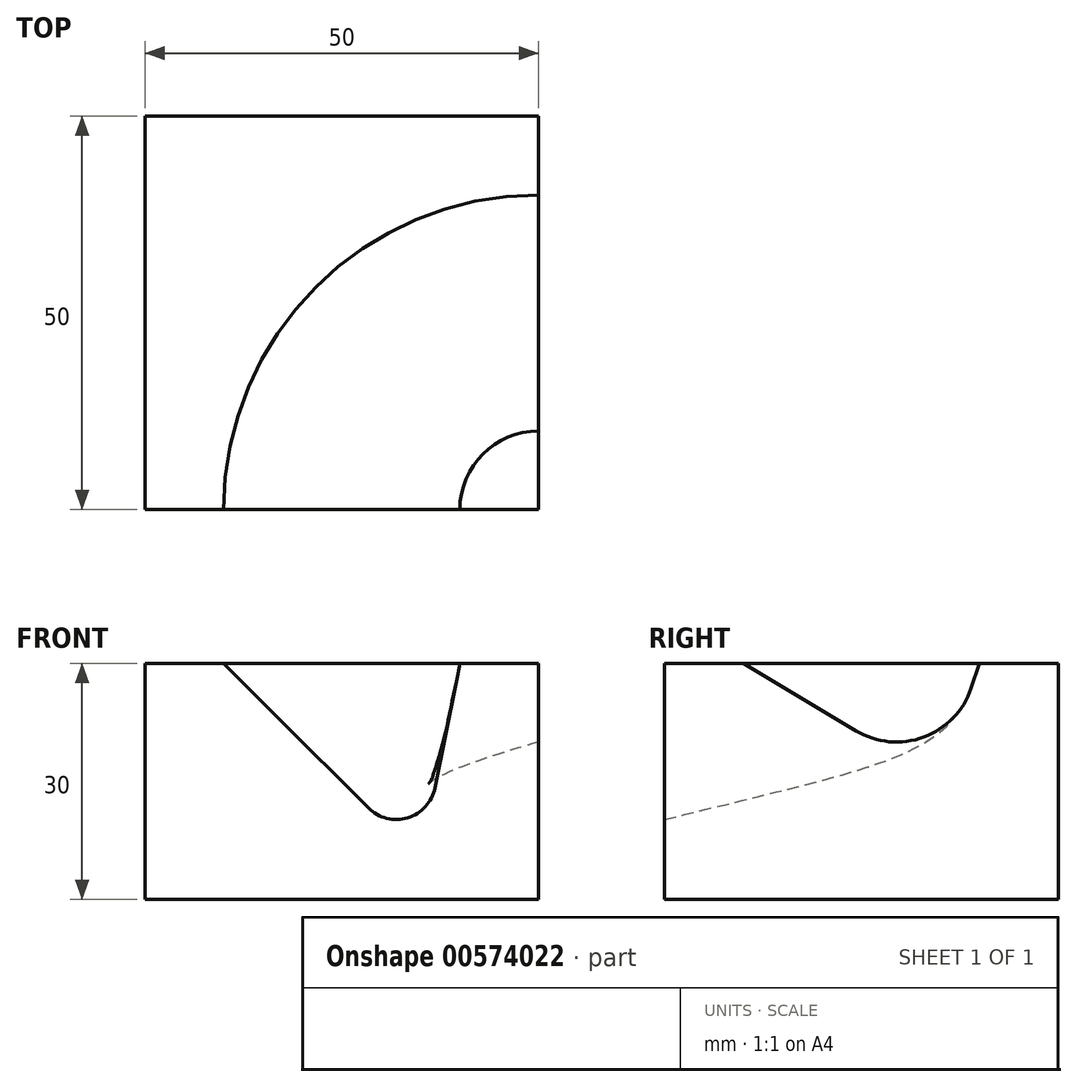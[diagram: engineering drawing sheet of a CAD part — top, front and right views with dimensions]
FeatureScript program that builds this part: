
annotation { "Feature Type Name" : "Feature", "Feature Type Description" : "" }
export const myFeature = defineFeature(function(context is Context, id is Id, definition is map)
    precondition{}
    {
        {
            var Q0;
            Q0=qCreatedBy(makeId("Front.planeOp"),FACE);
            var sketch = newSketch(context, id + "F0", { "sketchPlane" : qUnion([Q0])});
            skLineSegment(sketch, "E0.bottom", {"start": v(0, 30) * mm, "end": v(50, 30) * mm});
            skLineSegment(sketch, "E0.top", {"start": v(0, 0) * mm, "end": v(50, 0) * mm});
            skLineSegment(sketch, "E0.left", {"start": v(0, 30) * mm, "end": v(0, 0) * mm});
            skLineSegment(sketch, "E0.right", {"start": v(50, 30) * mm, "end": v(50, 0) * mm});
            skSolve(sketch);
        }
        {
            var Q0;
            Q0 = qSketchRegion(id + "F0", true);
            extrude(context, id + "F1", {"entities" : qUnion([Q0]), "depth" : 50 * mm, "offsetDistance" : 25 * mm});
        }
        {
            var Q0;
            Q0=makeQuery(id+"F1.opExtrude","CAP_FACE",FACE,{"disambiguationData":[OSD([sQuery(id+"F0.wireOp",EDGE,"E0.bottom"),sQuery(id+"F0.wireOp",EDGE,"E0.top"),sQuery(id+"F0.wireOp",EDGE,"E0.left"),sQuery(id+"F0.wireOp",EDGE,"E0.right")])],"isStart":false});
            var sketch = newSketch(context, id + "F2", { "sketchPlane" : qUnion([Q0])});
            skLineSegment(sketch, "E1", {"start": v(10, 30) * mm, "end": v(28.4, 11.6) * mm});
            skLineSegment(sketch, "E2", {"start": v(40, 30) * mm, "end": v(36.83, 14.16) * mm});
            skPoint(sketch, "E3.visualSharp", {"position": v(35, 5) * mm});
            skArc(sketch, "E3.filletArc", {"start": v(28.4, 11.6) * mm, "mid": v(33.38, 10.36) * mm, "end": v(36.83, 14.16) * mm});
            skLineSegment(sketch, "E4", {"start": v(10, 30) * mm, "end": v(40, 30) * mm});
            skSolve(sketch);
        }
        {
            var Q0;
            Q0=makeQuery(id+"F1.opExtrude","SWEPT_FACE",FACE,{"disambiguationData":[OSD([sQuery(id+"F0.wireOp",EDGE,"E0.right")])]});
            var sketch = newSketch(context, id + "F3", { "sketchPlane" : qUnion([Q0])});
            skLineSegment(sketch, "E5", {"start": v(-40, 30) * mm, "end": v(-25.69, 21.41) * mm});
            skLineSegment(sketch, "E6", {"start": v(-11.06, 26.83) * mm, "end": v(-10, 30) * mm});
            skLineSegment(sketch, "E7", {"start": v(-10, 30) * mm, "end": v(-40, 30) * mm});
            skPoint(sketch, "E8.visualSharp", {"position": v(-15, 15) * mm});
            skArc(sketch, "E8.filletArc", {"start": v(-25.69, 21.41) * mm, "mid": v(-17.08, 20.6) * mm, "end": v(-11.06, 26.83) * mm});
            skSolve(sketch);
        }
        {
            var Q0;
            Q0=makeQuery(id+"F1.opExtrude","SWEPT_FACE",FACE,{"disambiguationData":[OSD([sQuery(id+"F0.wireOp",EDGE,"E0.bottom")])]});
            var sketch = newSketch(context, id + "F4", { "sketchPlane" : qUnion([Q0])});
            skArc(sketch, "E9", {"start": v(50, -40) * mm, "mid": v(42.93, -42.93) * mm, "end": v(40, -50) * mm});
            skSolve(sketch);
        }
        {
            var Q0;
            Q0=makeQuery(id+"F1.opExtrude","SWEPT_FACE",FACE,{"disambiguationData":[OSD([sQuery(id+"F0.wireOp",EDGE,"E0.bottom")])]});
            var sketch = newSketch(context, id + "F5", { "sketchPlane" : qUnion([Q0])});
            skArc(sketch, "E10", {"start": v(50, -10) * mm, "mid": v(21.72, -21.72) * mm, "end": v(10, -50) * mm});
            skSolve(sketch);
        }
        {
            var Q1;
            Q1=makeQuery(id+"F2.imprint","IMPRINT",FACE,{"disambiguationData":[TD([[makeQuery(id+"F2.imprint","IMPRINT",EDGE,{"derivedFrom":sQuery(id+"F2.wireOp",EDGE,"E1")}),1.0]])]});
            var Q2;
            Q2=makeQuery(id+"F3.imprint","IMPRINT",FACE,{"disambiguationData":[TD([[makeQuery(id+"F3.imprint","IMPRINT",EDGE,{"derivedFrom":sQuery(id+"F3.wireOp",EDGE,"E5")}),1.0]])]});
            var Q3;
            Q3=sQuery(id+"F5.wireOp",EDGE,"E10");
            var Q4;
            Q4=sQuery(id+"F4.wireOp",EDGE,"E9");
            loft(context, id + "F6", {"operationType" : NewBodyOperationType.REMOVE, "addGuides" : true, "sheetProfilesArray" : [{ "sheetProfileEntities" : qUnion([Q1]) }, { "sheetProfileEntities" : qUnion([Q2]) }], "guidesArray" : [{ "guideEntities" : qUnion([Q3]), "guideDerivativeType" : LoftGuideDerivativeType.DEFAULT, "guideDerivativeMagnitude" : 1 }, { "guideEntities" : qUnion([Q4]), "guideDerivativeType" : LoftGuideDerivativeType.DEFAULT, "guideDerivativeMagnitude" : 1 }]});
        }
    });
